# Revit family: 94007113
name_source: partatom
category: Modelos genéricos
revit_build: Autodesk Revit 2016 (Build: 20150220_1215(x64)
units: mm (PartAtom-declared; Revit-internal decimal feet)

## family parameters
Com base no plano de trabalho = Não
Compartilhado = Não
Corte com vazios quando carregados = Não
Cota do conector redondo = Utilizar diâmetro
Pode hospedar o vergalhão = Não
Ponto de cálculo do ambiente = Não
Sempre na vertical = Sim
Tipo de parte = Normal

## types (1)
- Tramontina Cubas Undermount Quadrum 50 U - 94007-113
    Comentários de tipos = Instalação Apenas por baixo
    Código de montagem = 94007-113
    Descrição = Tramontina Cubas Undermount Quadrum 50 U- 94007-113
    Desenvolvedor = Factory Cursos
    Diametro do cano de saida = 34
    Fabricante = Tramontina
    Manual de Instalação = Cubas Undermount Quadrum.png
    Modelo = Tramontina Design Collection - Cuba  Quadrum Undermount 50 U
    Site do desenvolvedor = www.factorycursos.com.br
    Tamanho (mm) = 540 X 440 X 200 (Profundidade)
    Tipo de imagem = Cubas Undermount Quadrum.png
    URL = www.tramontina.com.br
